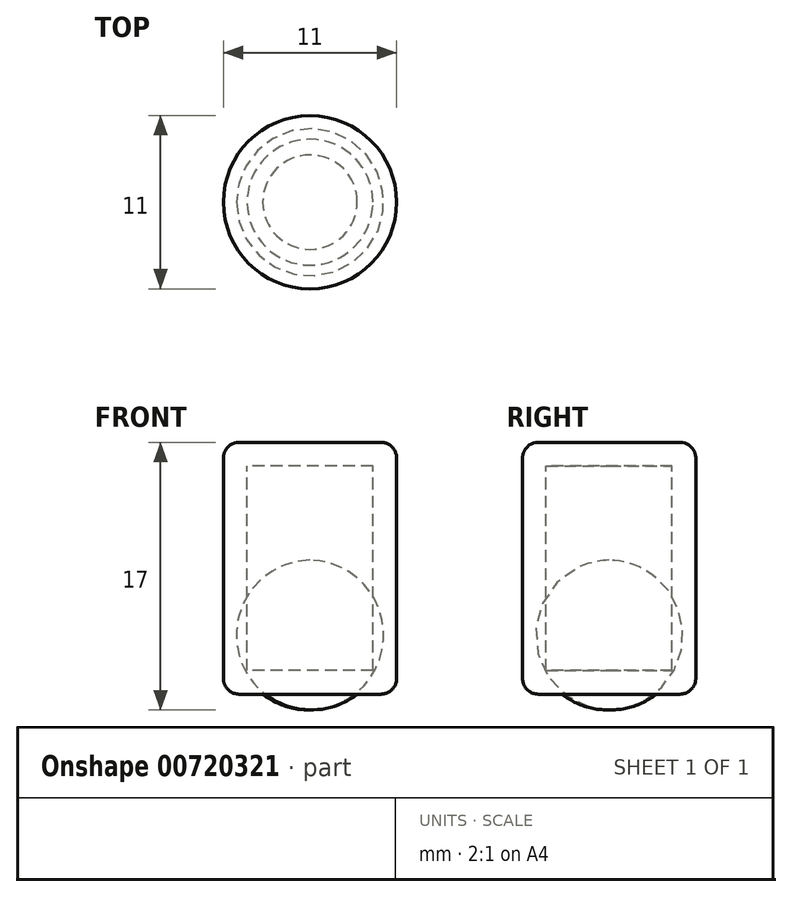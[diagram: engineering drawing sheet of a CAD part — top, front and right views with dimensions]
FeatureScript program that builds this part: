
annotation { "Feature Type Name" : "Feature", "Feature Type Description" : "" }
export const myFeature = defineFeature(function(context is Context, id is Id, definition is map)
    precondition{}
    {
        {
            var Q0;
            Q0=qCreatedBy(makeId("Top.planeOp"),FACE);
            var sketch = newSketch(context, id + "F0", { "sketchPlane" : qUnion([Q0])});
            skCircle(sketch, "E0", {"center": v(0, 0) * mm, "radius": 5.5 * mm});
            skSolve(sketch);
        }
        {
            var Q0;
            Q0=qSketchRegion(id+"F0",true);
            extrude(context, id + "F1", {"entities" : qUnion([Q0]), "oppositeDirection" : true, "depth" : 16 * mm, "offsetDistance" : 25 * mm});
        }
        {
            var Q0;
            Q0=makeQuery(id+"F1.opExtrude","CAP_EDGE",EDGE,{"disambiguationData":[OSD([sQuery(id+"F0.wireOp",EDGE,"E0")])],"isStart":false});
            fillet(context, id + "F2", {"entities" : qUnion([Q0]), "radius" : 1 * mm, "tangentPropagation" : true, "allowEdgeOverflow" : false});
        }
        {
            var Q0;
            Q0=makeQuery(id+"F1.opExtrude","SWEPT_FACE",FACE,{"disambiguationData":[OSD([sQuery(id+"F0.wireOp",EDGE,"E0")])]});
            var Q1;
            Q1=makeQuery(id+"F1.opExtrude","SWEPT_BODY",BODY,{"disambiguationData":[OSD([sQuery(id+"F0.wireOp",EDGE,"E0")])]});
            shell(context, id + "F3", {"isHollow" : true, "entities" : qUnion([Q0]), "parts" : qUnion([Q1]), "thickness" : 1.5 * mm});
        }
        {
            var Q0;
            Q0=qCreatedBy(makeId("Front.planeOp"),FACE);
            var sketch = newSketch(context, id + "F4", { "sketchPlane" : qUnion([Q0])});
            skLineSegment(sketch, "E1", {"start": v(0, -16) * mm, "end": v(3, -16) * mm});
            skLineSegment(sketch, "E2", {"start": v(0, -16) * mm, "end": v(0, -17) * mm});
            skArc(sketch, "E3", {"start": v(0, -17) * mm, "mid": v(1.59, -16.76) * mm, "end": v(3, -16) * mm});
            skSolve(sketch);
        }
        {
            var Q0;
            Q0=makeQuery(id+"F4.imprint","IMPRINT",FACE,{"disambiguationData":[TD([[makeQuery(id+"F4.imprint","IMPRINT",EDGE,{"derivedFrom":sQuery(id+"F4.wireOp",EDGE,"E1")}),-1.0]])]});
            var Q1;
            Q1=sQuery(id+"F4.wireOp",EDGE,"E2");
            revolve(context, id + "F5", {"operationType" : NewBodyOperationType.ADD, "surfaceOperationType" : NewSurfaceOperationType.NEW, "entities" : qUnion([Q0]), "axis" : qUnion([Q1]), "revolveType" : RevolveType.FULL});
        }
        {
            var Q0;
            Q0=makeQuery(id+"F1.opExtrude","CAP_EDGE",EDGE,{"disambiguationData":[OSD([sQuery(id+"F0.wireOp",EDGE,"E0")])],"isStart":true});
            fillet(context, id + "F6", {"entities" : qUnion([Q0]), "radius" : 1 * mm, "tangentPropagation" : true, "allowEdgeOverflow" : false});
        }
    });
